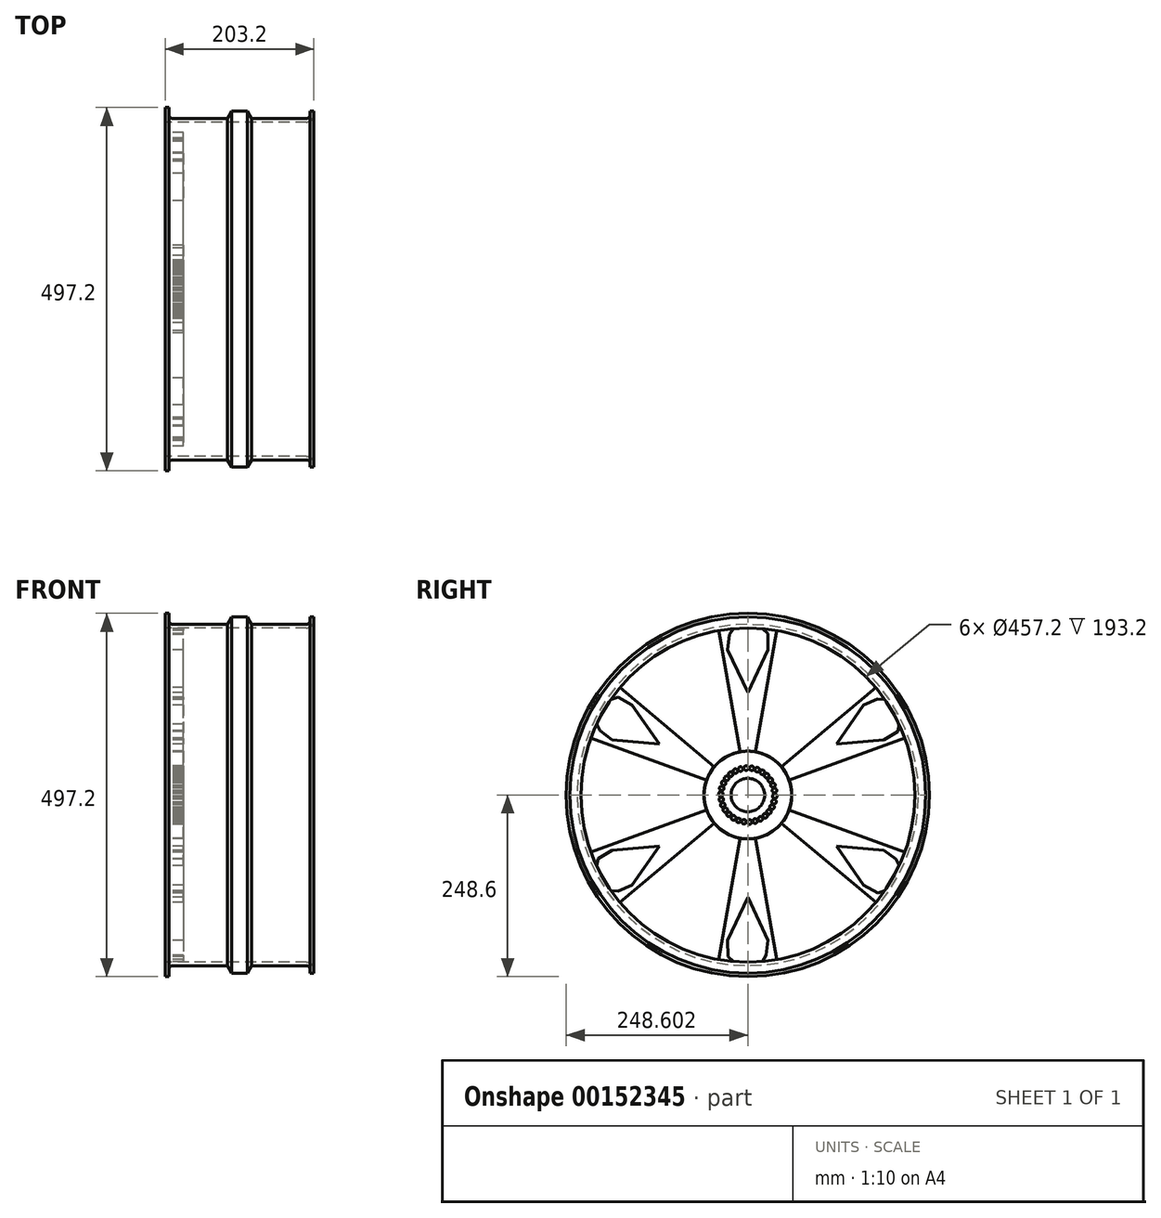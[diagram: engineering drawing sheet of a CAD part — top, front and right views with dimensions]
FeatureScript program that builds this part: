
annotation { "Feature Type Name" : "Feature", "Feature Type Description" : "" }
export const myFeature = defineFeature(function(context is Context, id is Id, definition is map)
    precondition{}
    {
        {
            var Q0;
            Q0=qCreatedBy(makeId("Top.planeOp"),FACE);
            var sketch = newSketch(context, id + "F0", { "sketchPlane" : qUnion([Q0])});
            skLineSegment(sketch, "E0", {"start": v(-79.7, 33.55) * mm, "end": v(113.5, 33.55) * mm});
            skLineSegment(sketch, "E1", {"start": v(-79.7, 33.55) * mm, "end": v(-79.7, 53.55) * mm});
            skLineSegment(sketch, "E2", {"start": v(123.5, 43.55) * mm, "end": v(123.5, 48.55) * mm});
            skLineSegment(sketch, "E3", {"start": v(-79.7, 53.55) * mm, "end": v(-74.7, 53.55) * mm});
            skLineSegment(sketch, "E4", {"start": v(-74.7, 53.55) * mm, "end": v(-74.7, 43.55) * mm});
            skLineSegment(sketch, "E5", {"start": v(-69.7, 38.55) * mm, "end": v(113.5, 38.55) * mm});
            skLineSegment(sketch, "E6", {"start": v(118.5, 43.55) * mm, "end": v(118.5, 48.55) * mm});
            skLineSegment(sketch, "E7", {"start": v(118.5, 48.55) * mm, "end": v(123.5, 48.55) * mm});
            skPoint(sketch, "E8.visualSharp", {"position": v(-74.7, 38.55) * mm});
            skArc(sketch, "E8.filletArc", {"start": v(-74.7, 43.55) * mm, "mid": v(-73.25, 40.02) * mm, "end": v(-69.7, 38.55) * mm});
            skPoint(sketch, "E9.visualSharp", {"position": v(118.5, 38.55) * mm});
            skArc(sketch, "E9.filletArc", {"start": v(113.5, 38.55) * mm, "mid": v(117.03, 40.02) * mm, "end": v(118.5, 43.55) * mm});
            skPoint(sketch, "E10.visualSharp", {"position": v(123.5, 33.55) * mm});
            skArc(sketch, "E10.filletArc", {"start": v(113.5, 33.55) * mm, "mid": v(120.56, 36.48) * mm, "end": v(123.5, 43.55) * mm});
            skLineSegment(sketch, "E11", {"start": v(-79.7, -195.05) * mm, "end": v(123.5, -195.05) * mm, "construction": true});
            skLineSegment(sketch, "E12", {"start": v(5.3, 38.55) * mm, "end": v(11.06, 48.55) * mm});
            skLineSegment(sketch, "E13", {"start": v(11.06, 48.55) * mm, "end": v(32.72, 48.55) * mm});
            skLineSegment(sketch, "E14", {"start": v(32.72, 48.55) * mm, "end": v(38.5, 38.55) * mm});
            skSolve(sketch);
        }
        {
            var Q0;
            Q0=makeQuery(id+"F0.imprint","IMPRINT",FACE,{"disambiguationData":[TD([[makeQuery(id+"F0.imprint","IMPRINT",EDGE,{"derivedFrom":sQuery(id+"F0.wireOp",EDGE,"E0")}),1.0]])]});
            var Q1;
            {var subQ0=sQuery(id+"F0.wireOp",EDGE,"E12");Q1=makeQuery(id+"F0.imprint","IMPRINT",FACE,{"disambiguationData":[TD([[makeQuery(id+"F0.imprint","IMPRINT",EDGE,{"derivedFrom":subQ0}),-1.0]])]});}
            var Q2;
            Q2=sQuery(id+"F0.wireOp",EDGE,"E11");
            revolve(context, id + "F1", {"entities" : qUnion([Q0, Q1]), "axis" : qUnion([Q2]), "revolveType" : RevolveType.FULL});
        }
        {
            var Q0;
            Q0=makeQuery(id+"F1.opRevolve","SWEPT_FACE",FACE,{"disambiguationData":[OSD([sQuery(id+"F0.wireOp",EDGE,"E1")])]});
            var sketch = newSketch(context, id + "F2", { "sketchPlane" : qUnion([Q0])});
            skCircle(sketch, "E15", {"center": v(195.05, 0) * mm, "radius": 22.92 * mm});
            skLineSegment(sketch, "E16", {"start": v(195.05, 60) * mm, "end": v(195.05, 140) * mm});
            skLineSegment(sketch, "E17", {"start": v(205.47, 59.09) * mm, "end": v(234.74, 225.13) * mm});
            skLineSegment(sketch, "E18", {"start": v(184.63, 59.09) * mm, "end": v(155.35, 225.13) * mm});
            skLineSegment(sketch, "E19", {"start": v(167.58, 198.9) * mm, "end": v(195.05, 140) * mm});
            skLineSegment(sketch, "E20", {"start": v(195.05, 140) * mm, "end": v(222.52, 198.9) * mm});
            skLineSegment(sketch, "E21", {"start": v(167.8, 221.2) * mm, "end": v(175.35, 227.75) * mm});
            skLineSegment(sketch, "E22", {"start": v(220.14, 219.33) * mm, "end": v(214.74, 227.75) * mm});
            skLineSegment(sketch, "E23", {"start": v(167.58, 198.9) * mm, "end": v(167.8, 221.2) * mm});
            skLineSegment(sketch, "E24", {"start": v(222.52, 198.9) * mm, "end": v(220.14, 219.33) * mm});
            skPoint(sketch, "E25.orphan", {"position": v(160.24, 214.65) * mm});
            skCircle(sketch, "E26", {"center": v(195.05, 0) * mm, "radius": 60 * mm});
            skCircle(sketch, "E27.1.0", {"center": v(-74.75, 141.61) * mm, "radius": 6 * mm});
            skPoint(sketch, "E27.center", {"position": v(0, 0) * mm});
            skCircle(sketch, "E28", {"center": v(158.16, -1.5) * mm, "radius": 3.11 * mm});
            skCircle(sketch, "E29.1.0", {"center": v(182.22, 34.62) * mm, "radius": 3.11 * mm});
            skCircle(sketch, "E29.2.0", {"center": v(224, 22.9) * mm, "radius": 3.11 * mm});
            skCircle(sketch, "E29.3.0", {"center": v(225.78, -20.47) * mm, "radius": 3.11 * mm});
            skCircle(sketch, "E29.4.0", {"center": v(185.08, -35.55) * mm, "radius": 3.11 * mm});
            skLineSegment(sketch, "E29.anchor1", {"start": v(195.05, 0) * mm, "end": v(158.16, -1.5) * mm, "construction": true});
            skLineSegment(sketch, "E29.anchor2", {"start": v(195.05, 0) * mm, "end": v(185.08, -35.55) * mm, "construction": true});
            skSolve(sketch);
        }
        {
            var Q0;
            {var subQ1=sQuery(id+"F2.wireOp",EDGE,"E16");Q0=makeQuery(id+"F2.imprint","IMPRINT",FACE,{"disambiguationData":[TD([[makeQuery(id+"F2.imprint","IMPRINT",EDGE,{"derivedFrom":subQ1}),1.0]])]});}
            var Q1;
            {var subQ1=sQuery(id+"F2.wireOp",EDGE,"E16");Q1=makeQuery(id+"F2.imprint","IMPRINT",FACE,{"disambiguationData":[TD([[makeQuery(id+"F2.imprint","IMPRINT",EDGE,{"derivedFrom":subQ1}),-1.0]])]});}
            var Q2;
            {var subQ0=sQuery(id+"F2.wireOp",EDGE,"E15");var subQ1=makeQuery(id+"F2.imprint","INTERSECT",VERTEX,{"derivedFrom":[subQ0,sQuery(id+"F2.wireOp",EDGE,"E16")]});Q2=makeQuery(id+"F2.imprint","IMPRINT",FACE,{"disambiguationData":[TD([[makeQuery(id+"F2.imprint","IMPRINT",EDGE,{"disambiguationData":[TD([[subQ1,1.0]])],"derivedFrom":subQ0}),1.0]])]});}
            var Q3;
            Q3=makeQuery(id+"F2.imprint","IMPRINT",FACE,{"disambiguationData":[TD([[makeQuery(id+"F2.imprint","IMPRINT",EDGE,{"derivedFrom":sQuery(id+"F2.wireOp",EDGE,"E15")}),-1.0]])]});
            extrude(context, id + "F3", {"entities" : qUnion([Q0, Q1, Q2, Q3]), "operationType" : NewBodyOperationType.ADD, "oppositeDirection" : true, "depth" : 25 * mm});
        }
        {
            var Q0;
            Q0=makeQuery(id+"F1.opRevolve","SWEPT_BODY",BODY,{"disambiguationData":[OSD([sQuery(id+"F0.wireOp",EDGE,"E0"),sQuery(id+"F0.wireOp",EDGE,"E1"),sQuery(id+"F0.wireOp",EDGE,"E2"),sQuery(id+"F0.wireOp",EDGE,"E3"),sQuery(id+"F0.wireOp",EDGE,"E4"),sQuery(id+"F0.wireOp",EDGE,"E5"),sQuery(id+"F0.wireOp",EDGE,"E6"),sQuery(id+"F0.wireOp",EDGE,"E7"),sQuery(id+"F0.wireOp",EDGE,"E8.filletArc"),sQuery(id+"F0.wireOp",EDGE,"E9.filletArc"),sQuery(id+"F0.wireOp",EDGE,"E10.filletArc"),sQuery(id+"F0.wireOp",EDGE,"E12"),sQuery(id+"F0.wireOp",EDGE,"E13"),sQuery(id+"F0.wireOp",EDGE,"E14")])]});
            var Q1;
            Q1=sQuery(id+"F0.wireOp",EDGE,"E11");
            circularPattern(context, id + "F4", {"entities" : qUnion([Q0]), "axis" : qUnion([Q1]), "angle" : 360 * degree, "instanceCount" : 6, "equalSpace" : true});
        }
        {
            var Q0;
            Q0=makeQuery(id+"F2.imprint","IMPRINT",FACE,{"disambiguationData":[TD([[makeQuery(id+"F2.imprint","IMPRINT",EDGE,{"derivedFrom":sQuery(id+"F2.wireOp",EDGE,"E28")}),1.0]])]});
            var Q1;
            Q1=makeQuery(id+"F2.imprint","IMPRINT",FACE,{"disambiguationData":[TD([[makeQuery(id+"F2.imprint","IMPRINT",EDGE,{"derivedFrom":sQuery(id+"F2.wireOp",EDGE,"E29.1.0")}),1.0]])]});
            var Q2;
            Q2=makeQuery(id+"F2.imprint","IMPRINT",FACE,{"disambiguationData":[TD([[makeQuery(id+"F2.imprint","IMPRINT",EDGE,{"derivedFrom":sQuery(id+"F2.wireOp",EDGE,"E29.2.0")}),1.0]])]});
            var Q3;
            Q3=makeQuery(id+"F2.imprint","IMPRINT",FACE,{"disambiguationData":[TD([[makeQuery(id+"F2.imprint","IMPRINT",EDGE,{"derivedFrom":sQuery(id+"F2.wireOp",EDGE,"E29.3.0")}),1.0]])]});
            var Q4;
            Q4=makeQuery(id+"F2.imprint","IMPRINT",FACE,{"disambiguationData":[TD([[makeQuery(id+"F2.imprint","IMPRINT",EDGE,{"derivedFrom":sQuery(id+"F2.wireOp",EDGE,"E29.4.0")}),1.0]])]});
            var Q5;
            Q5=makeQuery(id+"F2.imprint","IMPRINT",FACE,{"disambiguationData":[TD([[makeQuery(id+"F2.imprint","IMPRINT",EDGE,{"derivedFrom":sQuery(id+"F2.wireOp",EDGE,"E15")}),1.0]])]});
            extrude(context, id + "F5", {"entities" : qUnion([Q0, Q1, Q2, Q3, Q4, Q5]), "operationType" : NewBodyOperationType.REMOVE, "oppositeDirection" : true, "depth" : 25 * mm});
        }
    });
